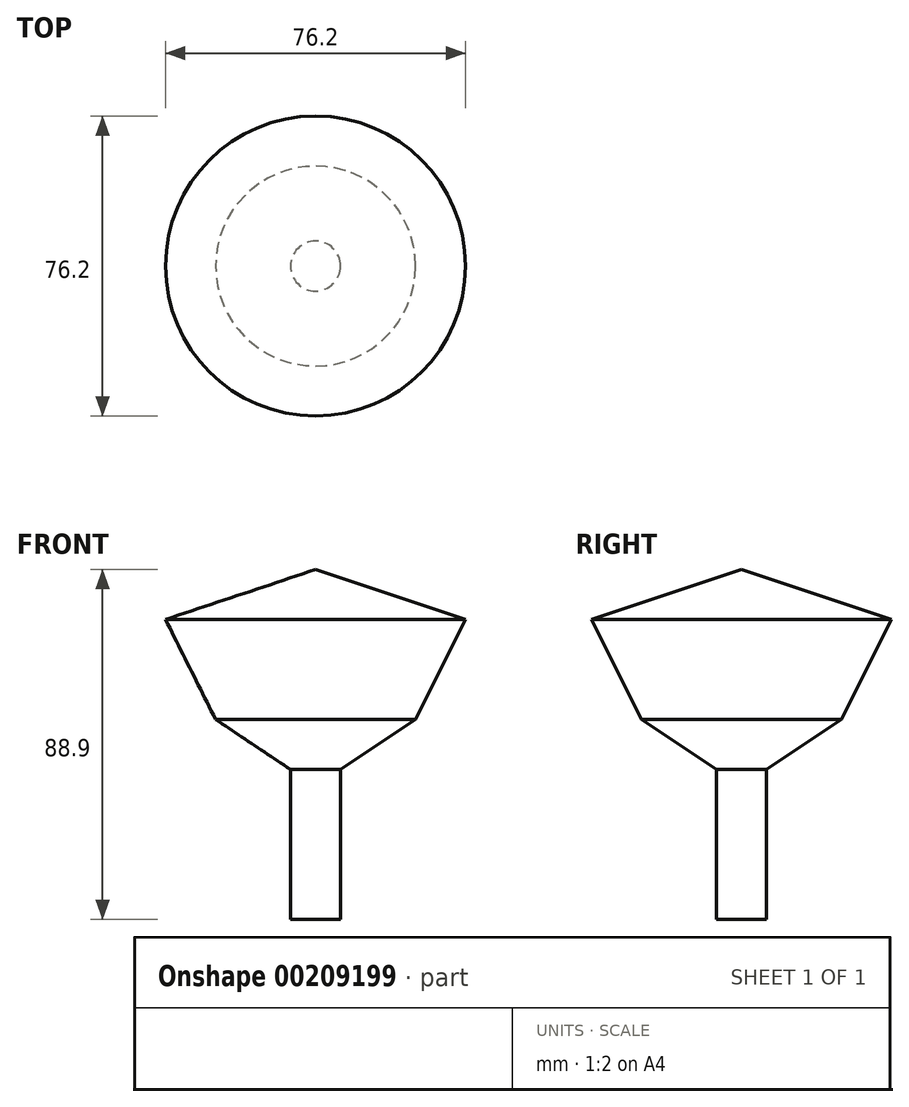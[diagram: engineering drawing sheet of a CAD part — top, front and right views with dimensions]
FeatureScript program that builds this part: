
annotation { "Feature Type Name" : "Feature", "Feature Type Description" : "" }
export const myFeature = defineFeature(function(context is Context, id is Id, definition is map)
    precondition{}
    {
        {
            var Q0;
            Q0=qCreatedBy(makeId("Front.planeOp"),FACE);
            var sketch = newSketch(context, id + "F0", { "sketchPlane" : qUnion([Q0])});
            skLineSegment(sketch, "E0", {"start": v(0, 0) * mm, "end": v(0, 88.9) * mm});
            skLineSegment(sketch, "E1", {"start": v(0, 88.9) * mm, "end": v(38.1, 76.2) * mm});
            skLineSegment(sketch, "E2", {"start": v(38.1, 76.2) * mm, "end": v(25.4, 50.8) * mm});
            skLineSegment(sketch, "E3", {"start": v(25.4, 50.8) * mm, "end": v(6.35, 38.1) * mm});
            skLineSegment(sketch, "E4", {"start": v(6.35, 38.1) * mm, "end": v(6.35, 0) * mm});
            skLineSegment(sketch, "E5", {"start": v(6.35, 0) * mm, "end": v(0, 0) * mm});
            skSolve(sketch);
        }
        {
            var Q0;
            Q0 = qSketchRegion(id + "F0", true);
            var Q1;
            Q1=sQuery(id+"F0.wireOp",EDGE,"E0");
            revolve(context, id + "F1", {"entities" : qUnion([Q0]), "axis" : qUnion([Q1]), "revolveType" : RevolveType.FULL});
        }
    });
